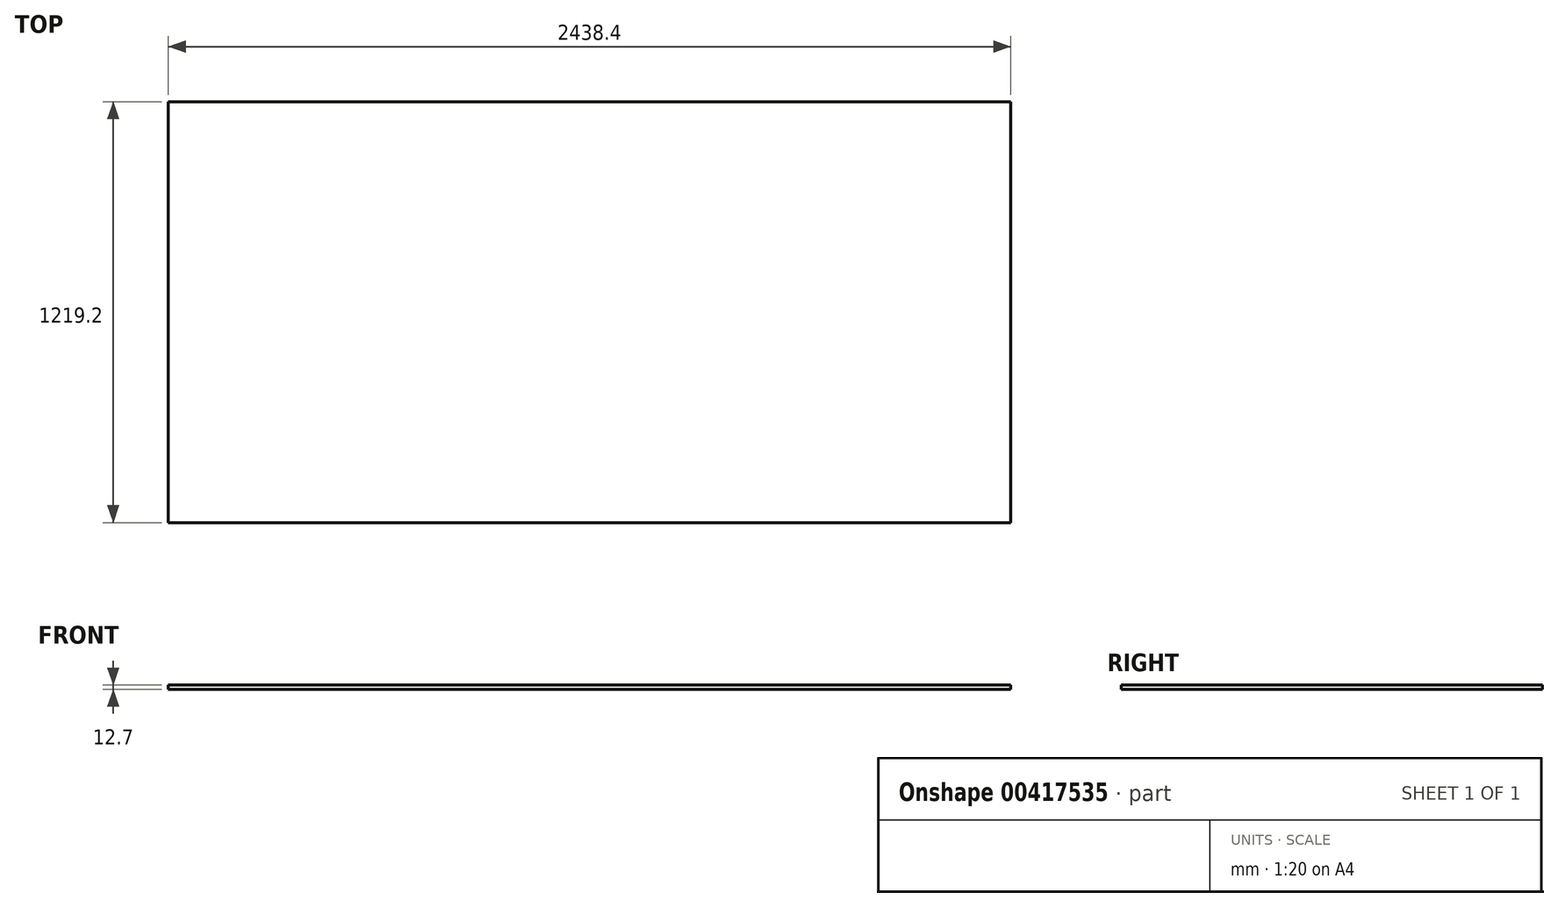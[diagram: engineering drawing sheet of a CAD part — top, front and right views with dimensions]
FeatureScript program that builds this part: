
annotation { "Feature Type Name" : "Feature", "Feature Type Description" : "" }
export const myFeature = defineFeature(function(context is Context, id is Id, definition is map)
    precondition{}
    {
        {
            var Q0;
            Q0=qCreatedBy(makeId("Top.planeOp"),FACE);
            var sketch = newSketch(context, id + "F0", { "sketchPlane" : qUnion([Q0])});
            skLineSegment(sketch, "E0.bottom", {"start": v(-1219.2, 609.6) * mm, "end": v(1219.2, 609.6) * mm});
            skLineSegment(sketch, "E0.top", {"start": v(-1219.2, -609.6) * mm, "end": v(1219.2, -609.6) * mm});
            skLineSegment(sketch, "E0.left", {"start": v(-1219.2, 609.6) * mm, "end": v(-1219.2, -609.6) * mm});
            skLineSegment(sketch, "E0.right", {"start": v(1219.2, 609.6) * mm, "end": v(1219.2, -609.6) * mm});
            skPoint(sketch, "E0.middle", {"position": v(0, 0) * mm});
            skSolve(sketch);
        }
        {
            var Q0;
            Q0 = qSketchRegion(id + "F0", true);
            extrude(context, id + "F1", {"entities" : qUnion([Q0]), "depth" : 12.7 * mm});
        }
    });
